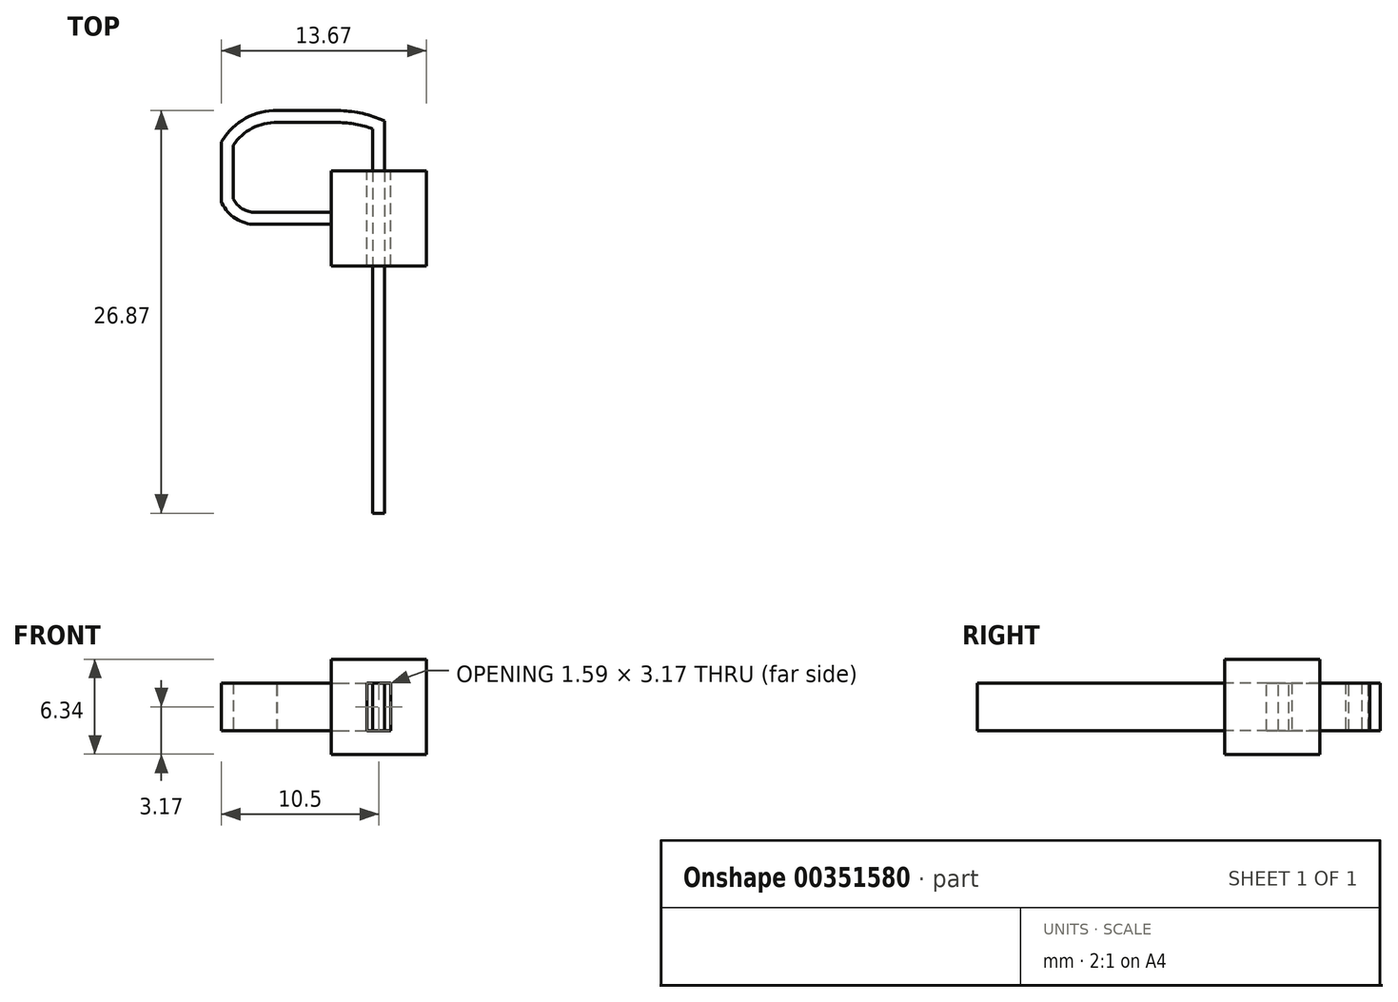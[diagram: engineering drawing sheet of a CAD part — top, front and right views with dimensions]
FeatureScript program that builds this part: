
annotation { "Feature Type Name" : "Feature", "Feature Type Description" : "" }
export const myFeature = defineFeature(function(context is Context, id is Id, definition is map)
    precondition{}
    {
        {
            var Q0;
            Q0=qCreatedBy(makeId("Top.planeOp"),FACE);
            var sketch = newSketch(context, id + "F0", { "sketchPlane" : qUnion([Q0])});
            skLineSegment(sketch, "E0.bottom", {"start": v(3.18, -3.18) * mm, "end": v(-3.18, -3.18) * mm});
            skLineSegment(sketch, "E0.top", {"start": v(3.18, 3.18) * mm, "end": v(-3.18, 3.17) * mm});
            skLineSegment(sketch, "E0.left", {"start": v(3.18, -3.18) * mm, "end": v(3.18, 3.18) * mm});
            skLineSegment(sketch, "E0.right", {"start": v(-3.18, -3.18) * mm, "end": v(-3.18, 3.18) * mm});
            skPoint(sketch, "E0.middle", {"position": v(0, 0) * mm});
            skSolve(sketch);
        }
        {
            var Q0;
            Q0 = qSketchRegion(id + "F0", true);
            extrude(context, id + "F1", {"entities" : qUnion([Q0]), "depth" : 6.35 * mm, "symmetric" : true});
        }
        {
            var Q0;
            Q0=makeQuery(id+"F1.opExtrude","SWEPT_FACE",FACE,{"disambiguationData":[OSD([sQuery(id+"F0.wireOp",EDGE,"E0.right")])]});
            var sketch = newSketch(context, id + "F2", { "sketchPlane" : qUnion([Q0])});
            skLineSegment(sketch, "E1.bottom", {"start": v(-0.4, -1.59) * mm, "end": v(0.4, -1.59) * mm});
            skLineSegment(sketch, "E1.top", {"start": v(-0.4, 1.59) * mm, "end": v(0.4, 1.59) * mm});
            skLineSegment(sketch, "E1.left", {"start": v(-0.4, -1.59) * mm, "end": v(-0.4, 1.59) * mm});
            skLineSegment(sketch, "E1.right", {"start": v(0.4, -1.59) * mm, "end": v(0.4, 1.59) * mm});
            skPoint(sketch, "E1.middle", {"position": v(0, 0) * mm});
            skSolve(sketch);
        }
        {
            var Q0;
            Q0=qCreatedBy(makeId("Top.planeOp"),FACE);
            var sketch = newSketch(context, id + "F3", { "sketchPlane" : qUnion([Q0])});
            skLineSegment(sketch, "E2", {"start": v(-8.23, 0) * mm, "end": v(-3.18, 0) * mm});
            skLineSegment(sketch, "E3", {"start": v(0, 6.23) * mm, "end": v(0, -19.68) * mm});
            skArc(sketch, "E4", {"start": v(-8.23, 0) * mm, "mid": v(-9.34, 0.32) * mm, "end": v(-10.1, 1.2) * mm});
            skLineSegment(sketch, "E5", {"start": v(-10.1, 1.2) * mm, "end": v(-10.1, 4.98) * mm});
            skArc(sketch, "E6", {"start": v(-6.77, 6.8) * mm, "mid": v(-8.68, 6.34) * mm, "end": v(-10.1, 4.98) * mm});
            skLineSegment(sketch, "E7", {"start": v(-6.77, 6.8) * mm, "end": v(-2.72, 6.8) * mm});
            skArc(sketch, "E8", {"start": v(-2.72, 6.8) * mm, "mid": v(-1.33, 6.65) * mm, "end": v(0, 6.23) * mm});
            skSolve(sketch);
        }
        {
            var Q0;
            Q0=makeQuery(id+"F1.opExtrude","SWEPT_FACE",FACE,{"disambiguationData":[OSD([sQuery(id+"F0.wireOp",EDGE,"E0.top")])]});
            var sketch = newSketch(context, id + "F4", { "sketchPlane" : qUnion([Q0])});
            skLineSegment(sketch, "E9.bottom", {"start": v(-0.8, -1.59) * mm, "end": v(0.8, -1.59) * mm});
            skLineSegment(sketch, "E9.top", {"start": v(-0.8, 1.59) * mm, "end": v(0.8, 1.59) * mm});
            skLineSegment(sketch, "E9.left", {"start": v(-0.8, -1.59) * mm, "end": v(-0.8, 1.59) * mm});
            skLineSegment(sketch, "E9.right", {"start": v(0.8, -1.59) * mm, "end": v(0.8, 1.59) * mm});
            skPoint(sketch, "E9.middle", {"position": v(0, 0) * mm});
            skSolve(sketch);
        }
        {
            var Q0;
            Q0 = qSketchRegion(id + "F4", true);
            extrude(context, id + "F5", {"entities" : qUnion([Q0]), "operationType" : NewBodyOperationType.REMOVE, "endBound" : BoundingType.THROUGH_ALL, "oppositeDirection" : true, "depth" : 25.4 * mm});
        }
        {
            var Q0;
            Q0 = qSketchRegion(id + "F2", true);
            var Q1;
            Q1 = qConstructionFilter(qBodyType(qCreatedBy(id + "F3" ,EDGE), BodyType.WIRE), ConstructionObject.NO);
            sweep(context, id + "F6", {"operationType" : NewBodyOperationType.ADD, "profiles" : qUnion([Q0]), "path" : qUnion([Q1])});
        }
    });
